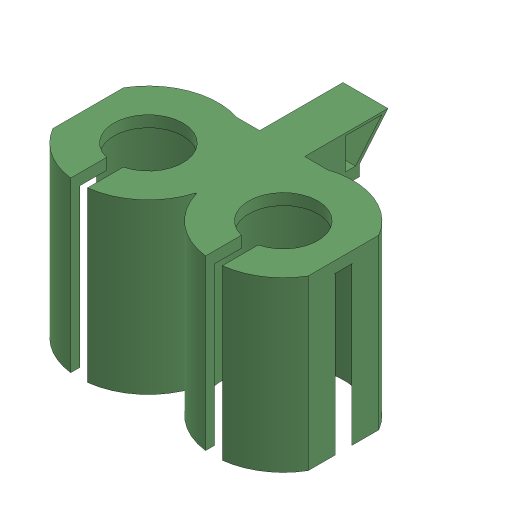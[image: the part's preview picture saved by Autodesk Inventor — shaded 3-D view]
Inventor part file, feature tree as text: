
AUTODESK INVENTOR PART (.ipt)
format: ipt  version: 2024.3 (Build 283343010, 343A)  size: 304,128 bytes
history: native  units: in
note: dims shown in document units (in); Inventor stores cm internally (conversion verified against a paired STEP export)
features: sketch x9, extrude x7, other x3, hole x1
ambient origin geometry x8: Origin, YZ Plane, XZ Plane, XY Plane, X Axis, Y Axis, Z Axis, Center Point
bodies: Solid1 (feature_tree)
feature tree (20):
  other  "main_manifold_8v_v02.ipt"
  other  "vial_ST_01.ipt"
  other  "mainPlate.ipt"
  sketch  "Sketch:VH: vials"  dims[d319=0.3in d1=0.3937in]
  sketch  "Sketch:VH: side cutout"  dims[d5=0.615in d8=0.1in d9=0.0in]
  extrude  "Ex: top of vials"  TaperAngle=0.0deg  [1 undecoded]
  extrude  "Ex: around vials"  Depth=0.3937in
  extrude  "Ex: side cutout"  Depth=0.1in TaperAngle=0.0deg
  extrude  "Ex: screw area"  Depth=1.4in
  sketch  "Sketch:VH: screw hole"  dims[d10=1.4in d11=0.0in d12=0.536in]
  hole  "Hole: screw to MP"  [1 undecoded]
  sketch  "Sketch:VH: extend front"  dims[d13=0.0in d14=0.0in d15=0.4in]
  extrude  "Ex: front cutout"  Depth=0.3in TaperAngle=0.0deg
  extrude  "Ex: under MP"  TaperAngle=0.0deg  [1 undecoded]
  extrude  "Extrusion12"  Depth=0.15in
  sketch  "Sketch:MM: flow sensor"  dims[d18=0.3635in d19=0.3in d20=0.0in]
  sketch  "Sketch:VH: screw part"  dims[d21=0.173in]
  sketch  "Sketch:VH: front cutout"  dims[d22=0.75in d23=0.375in d24=0.25in d25=0.5635in d26=0.21in d27=0.0in]
  sketch  "Sketch: under MP"  dims[d42=0.0in d43=0.0in d44=0.15in d47=0.02in d57=0.15in d58=0.2137in d59=0.3937in d297=0.175in d72=0.125in d75=0.1in d76=0.0in d77=0.126in d78=0.3436in d79=0.0421in d82=0.037in d83=0.1in d84=0.0in d85=0.0213in d86=0.0283in d87=0.0172in d89=0.2599in d90=0.2787in d91=0.089in d60=0.0344in d61=0.5in d62=0.0344in]
  sketch  "Sketch12"  dims[d0=0.3937in d439=0.0in]
note: 3 required parameter values undecoded (feature->parameter linkage not recoverable at this tier; creation-order binding heuristic only, values carry confidence <= 0.55)
